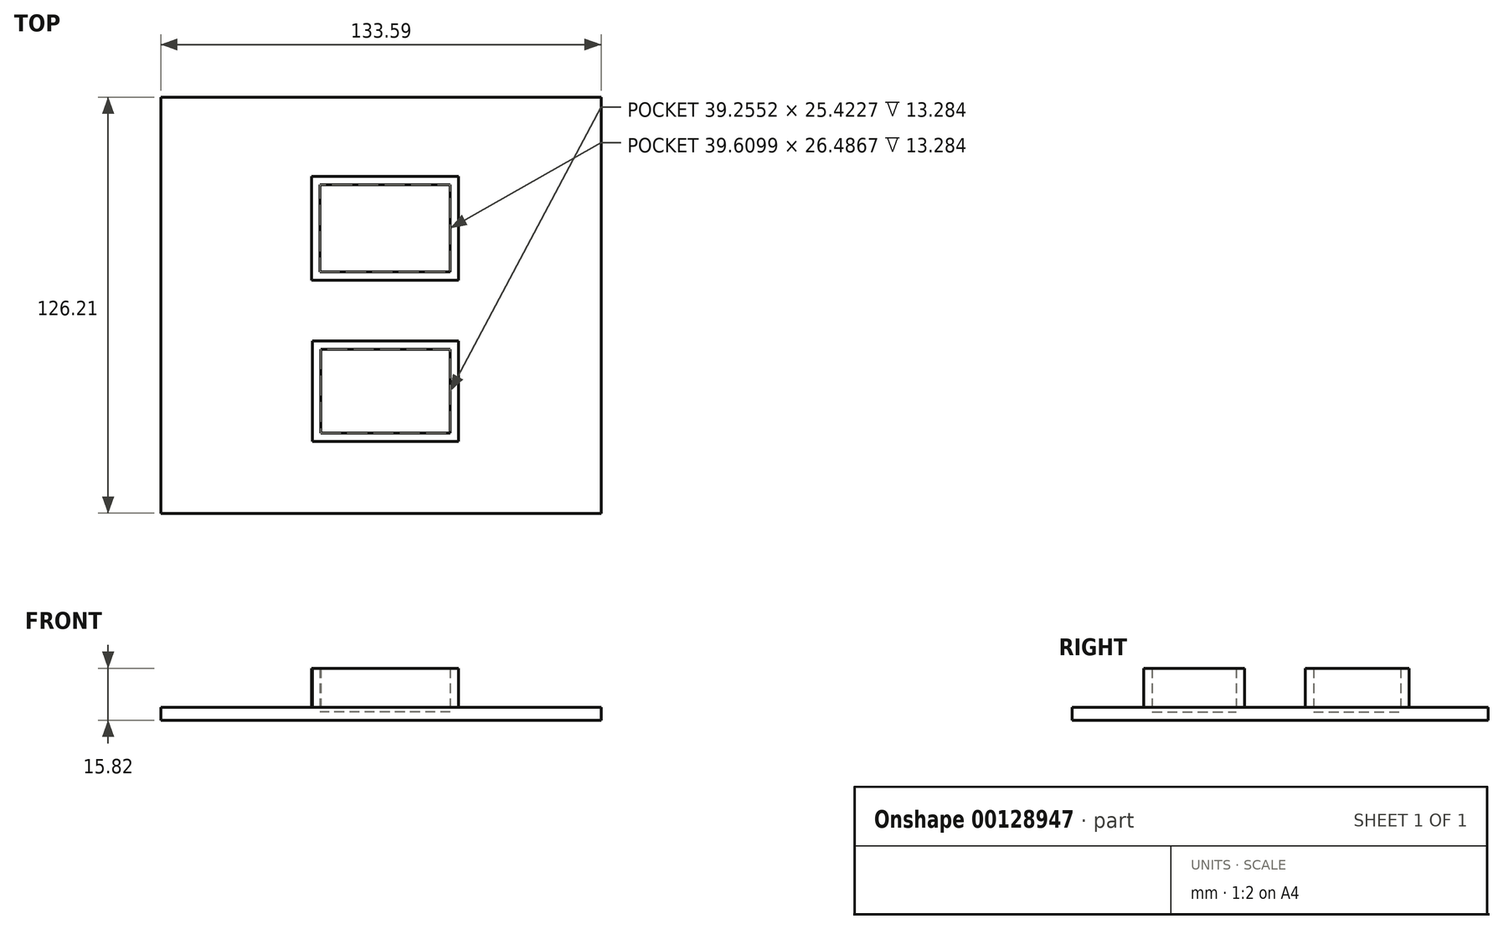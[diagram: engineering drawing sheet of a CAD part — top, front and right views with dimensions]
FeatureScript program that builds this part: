
annotation { "Feature Type Name" : "Feature", "Feature Type Description" : "" }
export const myFeature = defineFeature(function(context is Context, id is Id, definition is map)
    precondition{}
    {
        {
            var Q0;
            Q0=qCreatedBy(makeId("Top.planeOp"),FACE);
            var sketch = newSketch(context, id + "F0", { "sketchPlane" : qUnion([Q0])});
            skLineSegment(sketch, "E0.bottom", {"start": v(-67.4, 60.75) * mm, "end": v(66.18, 60.75) * mm});
            skLineSegment(sketch, "E0.top", {"start": v(-67.4, -65.46) * mm, "end": v(66.18, -65.46) * mm});
            skLineSegment(sketch, "E0.left", {"start": v(-67.4, 60.75) * mm, "end": v(-67.4, -65.46) * mm});
            skLineSegment(sketch, "E0.right", {"start": v(66.18, 60.75) * mm, "end": v(66.18, -65.46) * mm});
            skSolve(sketch);
        }
        {
            var Q0;
            Q0=makeQuery(id+"F0.imprint","IMPRINT",FACE,{"disambiguationData":[TD([[makeQuery(id+"F0.imprint","IMPRINT",EDGE,{"derivedFrom":sQuery(id+"F0.wireOp",EDGE,"E0.bottom")}),-1.0]])]});
            extrude(context, id + "F1", {"entities" : qUnion([Q0]), "depth" : 3.9 * mm});
        }
        {
            var Q0;
            Q0=makeQuery(id+"F1.opExtrude","CAP_FACE",FACE,{"disambiguationData":[OSD([sQuery(id+"F0.wireOp",EDGE,"E0.bottom"),sQuery(id+"F0.wireOp",EDGE,"E0.top"),sQuery(id+"F0.wireOp",EDGE,"E0.left"),sQuery(id+"F0.wireOp",EDGE,"E0.right")])],"isStart":false});
            var sketch = newSketch(context, id + "F2", { "sketchPlane" : qUnion([Q0])});
            skLineSegment(sketch, "E1.bottom", {"start": v(-21.72, 36.77) * mm, "end": v(22.97, 36.77) * mm});
            skLineSegment(sketch, "E1.top", {"start": v(-21.72, 5.2) * mm, "end": v(22.97, 5.2) * mm});
            skLineSegment(sketch, "E1.left", {"start": v(-21.72, 36.77) * mm, "end": v(-21.72, 5.2) * mm});
            skLineSegment(sketch, "E1.right", {"start": v(22.97, 36.77) * mm, "end": v(22.97, 5.2) * mm});
            skLineSegment(sketch, "E2.bottom", {"start": v(-21.37, -13.24) * mm, "end": v(22.97, -13.24) * mm});
            skLineSegment(sketch, "E2.top", {"start": v(-21.37, -43.74) * mm, "end": v(22.97, -43.74) * mm});
            skLineSegment(sketch, "E2.left", {"start": v(-21.37, -13.24) * mm, "end": v(-21.37, -43.74) * mm});
            skLineSegment(sketch, "E2.right", {"start": v(22.97, -13.24) * mm, "end": v(22.97, -43.74) * mm});
            skSolve(sketch);
        }
        {
            var Q0;
            Q0=makeQuery(id+"F2.imprint","IMPRINT",FACE,{"disambiguationData":[TD([[makeQuery(id+"F2.imprint","IMPRINT",EDGE,{"derivedFrom":sQuery(id+"F2.wireOp",EDGE,"E1.bottom")}),-1.0]])]});
            var Q1;
            Q1=makeQuery(id+"F2.imprint","IMPRINT",FACE,{"disambiguationData":[TD([[makeQuery(id+"F2.imprint","IMPRINT",EDGE,{"derivedFrom":sQuery(id+"F2.wireOp",EDGE,"E2.bottom")}),-1.0]])]});
            extrude(context, id + "F3", {"entities" : qUnion([Q0, Q1]), "operationType" : NewBodyOperationType.ADD, "depth" : 11.92 * mm});
        }
        {
            var Q0;
            Q0=makeQuery(id+"F3.opExtrude","CAP_FACE",FACE,{"disambiguationData":[OSD([sQuery(id+"F2.wireOp",EDGE,"E2.bottom"),sQuery(id+"F2.wireOp",EDGE,"E2.top"),sQuery(id+"F2.wireOp",EDGE,"E2.left"),sQuery(id+"F2.wireOp",EDGE,"E2.right")])],"isStart":false});
            var Q1;
            Q1=makeQuery(id+"F3.opExtrude","CAP_FACE",FACE,{"disambiguationData":[OSD([sQuery(id+"F2.wireOp",EDGE,"E1.bottom"),sQuery(id+"F2.wireOp",EDGE,"E1.top"),sQuery(id+"F2.wireOp",EDGE,"E1.left"),sQuery(id+"F2.wireOp",EDGE,"E1.right")])],"isStart":false});
            shell(context, id + "F4", {"entities" : qUnion([Q0, Q1]), "thickness" : 2.54 * mm});
        }
    });
